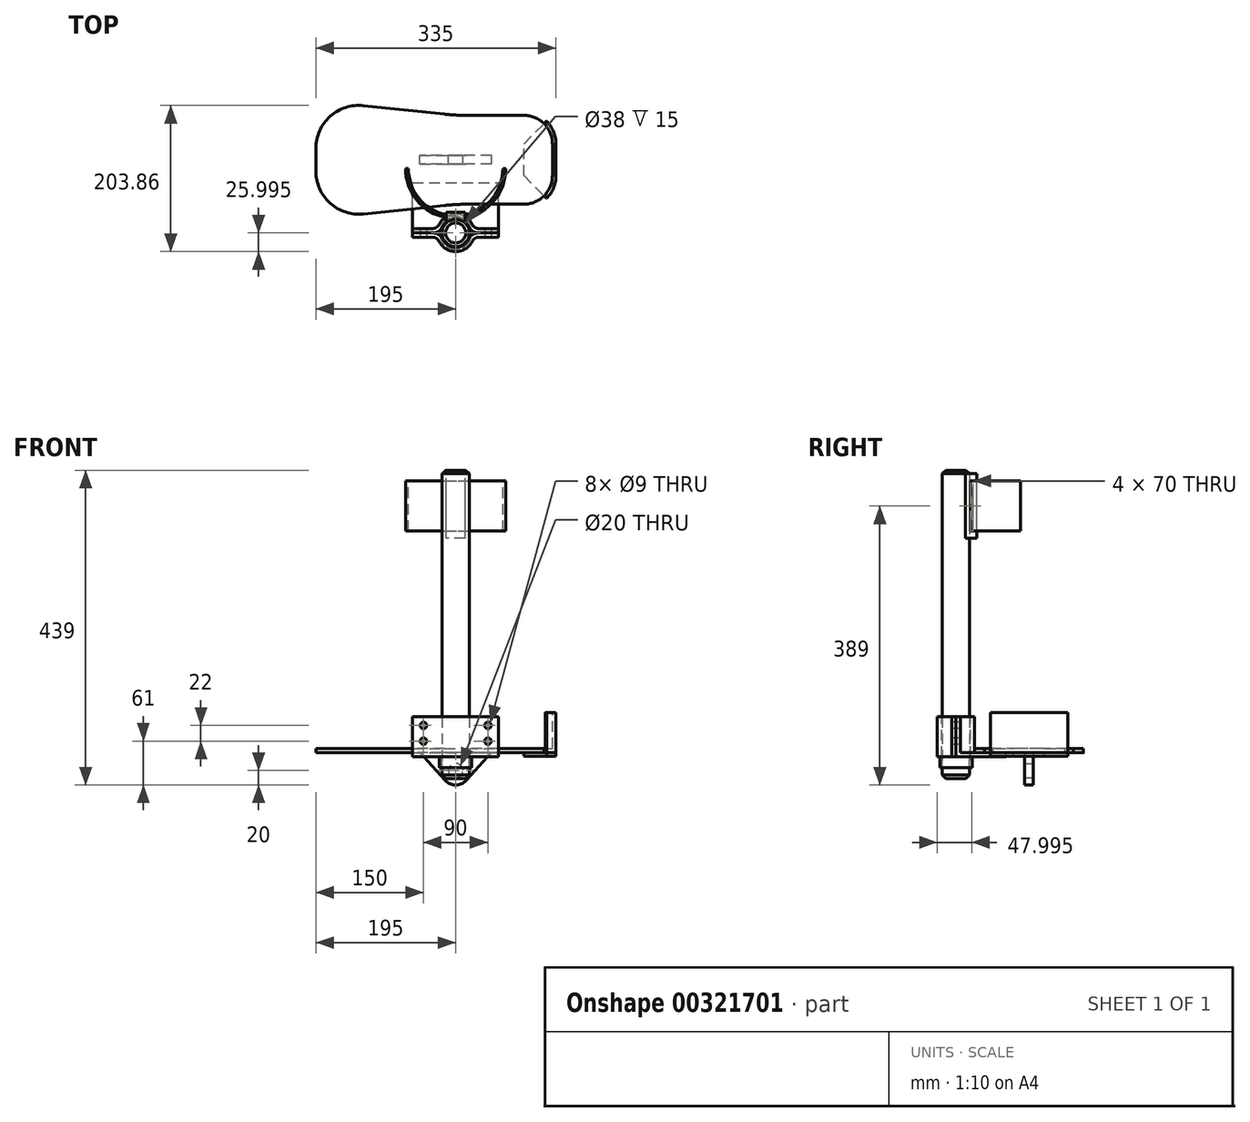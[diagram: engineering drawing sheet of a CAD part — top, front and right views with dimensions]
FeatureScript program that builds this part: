
annotation { "Feature Type Name" : "Feature", "Feature Type Description" : "" }
export const myFeature = defineFeature(function(context is Context, id is Id, definition is map)
    precondition{}
    {
        {
            var Q0;
            Q0=qCreatedBy(makeId("Top.planeOp"),FACE);
            var sketch = newSketch(context, id + "F0", { "sketchPlane" : qUnion([Q0])});
            skLineSegment(sketch, "E0", {"start": v(-175, 82.5) * mm, "end": v(-175, -82.5) * mm});
            skLineSegment(sketch, "E1", {"start": v(-175, 82.5) * mm, "end": v(20, 62) * mm});
            skLineSegment(sketch, "E2", {"start": v(20, 62) * mm, "end": v(155, 62) * mm});
            skLineSegment(sketch, "E3", {"start": v(155, 62) * mm, "end": v(155, -62) * mm});
            skLineSegment(sketch, "E4", {"start": v(155, -62) * mm, "end": v(20, -62) * mm});
            skLineSegment(sketch, "E5", {"start": v(20, -62) * mm, "end": v(-175, -82.5) * mm});
            skSolve(sketch);
        }
        {
            var Q0;
            Q0=makeQuery(id+"F0.imprint","IMPRINT",FACE,{"disambiguationData":[TD([[makeQuery(id+"F0.imprint","IMPRINT",EDGE,{"derivedFrom":sQuery(id+"F0.wireOp",EDGE,"E0")}),1.0]])]});
            extrude(context, id + "F1", {"entities" : qUnion([Q0]), "depth" : 6 * mm});
        }
        {
            var Q0;
            Q0=makeQuery(id+"F1.opExtrude","SWEPT_EDGE",EDGE,{"disambiguationData":[OSD([sQuery(id+"F0.wireOp",EDGE,"E0"),sQuery(id+"F0.wireOp",EDGE,"E5")])]});
            var Q1;
            Q1=makeQuery(id+"F1.opExtrude","SWEPT_EDGE",EDGE,{"disambiguationData":[OSD([sQuery(id+"F0.wireOp",EDGE,"E0"),sQuery(id+"F0.wireOp",EDGE,"E1")])]});
            fillet(context, id + "F2", {"entities" : qUnion([Q0, Q1]), "radius" : 60 * mm, "tangentPropagation" : true, "allowEdgeOverflow" : false});
        }
        {
            var Q0;
            Q0=makeQuery(id+"F1.opExtrude","SWEPT_EDGE",EDGE,{"disambiguationData":[OSD([sQuery(id+"F0.wireOp",EDGE,"E2"),sQuery(id+"F0.wireOp",EDGE,"E3")])]});
            var Q1;
            Q1=makeQuery(id+"F1.opExtrude","SWEPT_EDGE",EDGE,{"disambiguationData":[OSD([sQuery(id+"F0.wireOp",EDGE,"E3"),sQuery(id+"F0.wireOp",EDGE,"E4")])]});
            fillet(context, id + "F3", {"entities" : qUnion([Q0, Q1]), "radius" : 40 * mm, "tangentPropagation" : true, "allowEdgeOverflow" : false});
        }
        {
            var Q0;
            Q0=makeQuery(id+"F1.opExtrude","SWEPT_EDGE",EDGE,{"disambiguationData":[OSD([sQuery(id+"F0.wireOp",EDGE,"E4"),sQuery(id+"F0.wireOp",EDGE,"E5")])]});
            var Q1;
            Q1=makeQuery(id+"F1.opExtrude","SWEPT_EDGE",EDGE,{"disambiguationData":[OSD([sQuery(id+"F0.wireOp",EDGE,"E1"),sQuery(id+"F0.wireOp",EDGE,"E2")])]});
            fillet(context, id + "F4", {"entities" : qUnion([Q0, Q1]), "radius" : 300 * mm, "tangentPropagation" : true, "allowEdgeOverflow" : false});
        }
        {
            var Q0;
            Q0=qCreatedBy(makeId("Front.planeOp"),FACE);
            var sketch = newSketch(context, id + "F5", { "sketchPlane" : qUnion([Q0])});
            skArc(sketch, "E6", {"start": v(5.25, -38.5) * mm, "mid": v(20, -45) * mm, "end": v(34.75, -38.5) * mm});
            skLineSegment(sketch, "E7", {"start": v(20, -25) * mm, "end": v(20, 19.27) * mm, "construction": true});
            skLineSegment(sketch, "E8.0", {"start": v(70, -25) * mm, "end": v(70, 0) * mm, "construction": true});
            skLineSegment(sketch, "E9.0", {"start": v(-30, -25) * mm, "end": v(-30, 0) * mm, "construction": true});
            skLineSegment(sketch, "E10.0", {"start": v(70, 0) * mm, "end": v(-30, 0) * mm});
            skPoint(sketch, "E11.orphan", {"position": v(4.36, 0) * mm});
            skPoint(sketch, "E12.orphan", {"position": v(-108.73, 0) * mm});
            skLineSegment(sketch, "E13", {"start": v(-30, 0) * mm, "end": v(5.25, -38.5) * mm});
            skLineSegment(sketch, "E14", {"start": v(70, 0) * mm, "end": v(34.75, -38.5) * mm});
            skCircle(sketch, "E15", {"center": v(20, -25) * mm, "radius": 10 * mm});
            skSolve(sketch);
        }
        {
            var Q0;
            Q0=makeQuery(id+"F5.imprint","IMPRINT",FACE,{"disambiguationData":[TD([[makeQuery(id+"F5.imprint","IMPRINT",EDGE,{"derivedFrom":sQuery(id+"F5.wireOp",EDGE,"E6")}),1.0]])]});
            extrude(context, id + "F6", {"entities" : qUnion([Q0]), "operationType" : NewBodyOperationType.ADD, "endBound" : BoundingType.SYMMETRIC, "depth" : 12 * mm});
        }
        {
            var Q0;
            Q0=makeQuery(id+"F1.opExtrude","CAP_FACE",FACE,{"disambiguationData":[OSD([sQuery(id+"F0.wireOp",EDGE,"E0"),sQuery(id+"F0.wireOp",EDGE,"E1"),sQuery(id+"F0.wireOp",EDGE,"E2"),sQuery(id+"F0.wireOp",EDGE,"E3"),sQuery(id+"F0.wireOp",EDGE,"E4"),sQuery(id+"F0.wireOp",EDGE,"E5")])],"isStart":false});
            var sketch = newSketch(context, id + "F7", { "sketchPlane" : qUnion([Q0])});
            skLineSegment(sketch, "E16.0", {"start": v(155, 22) * mm, "end": v(155, -22) * mm});
            skArc(sketch, "E17.0", {"start": v(155, 22) * mm, "mid": v(151.96, 37.31) * mm, "end": v(143.28, 50.29) * mm});
            skArc(sketch, "E18.0", {"start": v(143.28, -50.29) * mm, "mid": v(151.96, -37.31) * mm, "end": v(155, -22) * mm});
            skLineSegment(sketch, "E19", {"start": v(143.28, 50.29) * mm, "end": v(146.82, 53.82) * mm});
            skLineSegment(sketch, "E20", {"start": v(143.28, -50.29) * mm, "end": v(146.82, -53.82) * mm});
            skPoint(sketch, "E21.orphan", {"position": v(115, 62) * mm});
            skPoint(sketch, "E22.orphan", {"position": v(115, -62) * mm});
            skArc(sketch, "E23.0", {"start": v(160, 22) * mm, "mid": v(156.57, 39.23) * mm, "end": v(146.82, 53.82) * mm});
            skLineSegment(sketch, "E23.1", {"start": v(160, 22) * mm, "end": v(160, -22) * mm});
            skArc(sketch, "E23.2", {"start": v(146.82, -53.82) * mm, "mid": v(156.57, -39.23) * mm, "end": v(160, -22) * mm});
            skSolve(sketch);
        }
        {
            var Q0;
            Q0=makeQuery(id+"F7.imprint","IMPRINT",FACE,{"disambiguationData":[TD([[makeQuery(id+"F7.imprint","IMPRINT",EDGE,{"derivedFrom":sQuery(id+"F7.wireOp",EDGE,"E16.0")}),1.0]])]});
            extrude(context, id + "F8", {"entities" : qUnion([Q0]), "oppositeDirection" : true, "depth" : 6 * mm});
        }
        {
            var Q0;
            Q0 = qSketchRegion(id + "F7", true);
            extrude(context, id + "F9", {"entities" : qUnion([Q0]), "operationType" : NewBodyOperationType.ADD, "depth" : 50 * mm});
        }
        {
            var Q0;
            {var subQ0=sQuery(id+"F7.wireOp",EDGE,"E20");var subQ1=sQuery(id+"F7.wireOp",EDGE,"E18.0");var subQ2=sQuery(id+"F0.wireOp",EDGE,"E5");var subQ3=sQuery(id+"F0.wireOp",EDGE,"E4");var subQ4=sQuery(id+"F0.wireOp",EDGE,"E3");var subQ5=sQuery(id+"F0.wireOp",EDGE,"E2");var subQ6=sQuery(id+"F0.wireOp",EDGE,"E1");var subQ7=sQuery(id+"F0.wireOp",EDGE,"E0");Q0=makeQuery(id+"F9.boolean.opBoolean","MERGE",EDGE,{"derivedFrom":[makeQuery(id+"F8.opExtrude","SWEPT_EDGE",EDGE,{"disambiguationData":[OSD([subQ7,subQ6,subQ5,subQ4,subQ3,subQ2,subQ1,subQ0])]}),makeQuery(id+"F9.opExtrude","SWEPT_EDGE",EDGE,{"disambiguationData":[OSD([subQ7,subQ6,subQ5,subQ4,subQ3,subQ2,subQ1,subQ0])]})]});}
            var Q1;
            {var subQ0=sQuery(id+"F7.wireOp",EDGE,"E19");var subQ1=sQuery(id+"F7.wireOp",EDGE,"E17.0");var subQ2=sQuery(id+"F0.wireOp",EDGE,"E5");var subQ3=sQuery(id+"F0.wireOp",EDGE,"E4");var subQ4=sQuery(id+"F0.wireOp",EDGE,"E3");var subQ5=sQuery(id+"F0.wireOp",EDGE,"E2");var subQ6=sQuery(id+"F0.wireOp",EDGE,"E1");var subQ7=sQuery(id+"F0.wireOp",EDGE,"E0");Q1=makeQuery(id+"F9.boolean.opBoolean","MERGE",EDGE,{"derivedFrom":[makeQuery(id+"F8.opExtrude","SWEPT_EDGE",EDGE,{"disambiguationData":[OSD([subQ7,subQ6,subQ5,subQ4,subQ3,subQ2,subQ1,subQ0])]}),makeQuery(id+"F9.opExtrude","SWEPT_EDGE",EDGE,{"disambiguationData":[OSD([subQ7,subQ6,subQ5,subQ4,subQ3,subQ2,subQ1,subQ0])]})]});}
            fillet(context, id + "F10", {"entities" : qUnion([Q0, Q1]), "radius" : 5 * mm, "tangentPropagation" : true, "allowEdgeOverflow" : false});
        }
        {
            var Q0;
            Q0=makeQuery(id+"F8.opExtrude","CAP_FACE",FACE,{"disambiguationData":[OSD([sQuery(id+"F7.wireOp",EDGE,"E16.0"),sQuery(id+"F7.wireOp",EDGE,"E17.0"),sQuery(id+"F7.wireOp",EDGE,"E18.0"),sQuery(id+"F7.wireOp",EDGE,"E19"),sQuery(id+"F7.wireOp",EDGE,"E20"),sQuery(id+"F7.wireOp",EDGE,"E23.0"),sQuery(id+"F7.wireOp",EDGE,"E23.1"),sQuery(id+"F7.wireOp",EDGE,"E23.2")])],"isStart":false});
            var sketch = newSketch(context, id + "F11", { "sketchPlane" : qUnion([Q0])});
            skArc(sketch, "E24.0", {"start": v(146.82, 53.82) * mm, "mid": v(156.57, 39.23) * mm, "end": v(160, 22) * mm});
            skLineSegment(sketch, "E25.0", {"start": v(160, -22) * mm, "end": v(160, 22) * mm});
            skArc(sketch, "E26.0", {"start": v(160, -22) * mm, "mid": v(156.57, -39.23) * mm, "end": v(146.82, -53.82) * mm});
            skLineSegment(sketch, "E27", {"start": v(115, 22) * mm, "end": v(146.82, 53.82) * mm});
            skLineSegment(sketch, "E28", {"start": v(115, 22) * mm, "end": v(115, -22) * mm});
            skLineSegment(sketch, "E29", {"start": v(115, -22) * mm, "end": v(146.82, -53.82) * mm});
            skSolve(sketch);
        }
        {
            var Q0;
            Q0 = qSketchRegion(id + "F11", true);
            extrude(context, id + "F12", {"entities" : qUnion([Q0]), "depth" : 5 * mm});
        }
        {
            var Q0;
            Q0=makeQuery(id+"F1.opExtrude","CAP_FACE",FACE,{"disambiguationData":[OSD([sQuery(id+"F0.wireOp",EDGE,"E0"),sQuery(id+"F0.wireOp",EDGE,"E1"),sQuery(id+"F0.wireOp",EDGE,"E2"),sQuery(id+"F0.wireOp",EDGE,"E3"),sQuery(id+"F0.wireOp",EDGE,"E4"),sQuery(id+"F0.wireOp",EDGE,"E5")])],"isStart":true});
            var sketch = newSketch(context, id + "F13", { "sketchPlane" : qUnion([Q0])});
            skLineSegment(sketch, "E30.bottom", {"start": v(-40, 102) * mm, "end": v(0, 102) * mm});
            skLineSegment(sketch, "E30.top", {"start": v(-40, 32) * mm, "end": v(80, 32) * mm});
            skLineSegment(sketch, "E30.left", {"start": v(-40, 102) * mm, "end": v(-40, 32) * mm});
            skLineSegment(sketch, "E30.right", {"start": v(80, 102) * mm, "end": v(80, 32) * mm});
            skArc(sketch, "E31", {"start": v(0, 102) * mm, "mid": v(20, 82) * mm, "end": v(40, 102) * mm});
            skLineSegment(sketch, "E32.trimOffspring", {"start": v(40, 102) * mm, "end": v(80, 102) * mm});
            skSolve(sketch);
        }
        {
            var Q0;
            {var subQ8=sQuery(id+"F13.wireOp",EDGE,"E30.bottom");Q0=makeQuery(id+"F13.imprint","IMPRINT",FACE,{"disambiguationData":[TD([[makeQuery(id+"F13.imprint","IMPRINT",EDGE,{"derivedFrom":subQ8}),-1.0]])]});}
            var Q1;
            {var subQ4=sQuery(id+"F13.wireOp",EDGE,"E30.top");Q1=makeQuery(id+"F13.imprint","IMPRINT",FACE,{"disambiguationData":[TD([[makeQuery(id+"F13.imprint","IMPRINT",EDGE,{"derivedFrom":subQ4}),1.0]])]});}
            extrude(context, id + "F14", {"entities" : qUnion([Q0, Q1]), "depth" : 6 * mm});
        }
        {
            var Q0;
            Q0=makeQuery(id+"F14.opExtrude","CAP_FACE",FACE,{"disambiguationData":[OSD([sQuery(id+"F13.wireOp",EDGE,"E30.bottom"),sQuery(id+"F13.wireOp",EDGE,"E30.top"),sQuery(id+"F13.wireOp",EDGE,"E30.left"),sQuery(id+"F13.wireOp",EDGE,"E30.right"),sQuery(id+"F13.wireOp",EDGE,"E31"),sQuery(id+"F13.wireOp",EDGE,"E32.trimOffspring")])],"isStart":true});
            var sketch = newSketch(context, id + "F15", { "sketchPlane" : qUnion([Q0])});
            skArc(sketch, "E33.0", {"start": v(0, -102) * mm, "mid": v(20, -82) * mm, "end": v(40, -102) * mm});
            skLineSegment(sketch, "E34.0", {"start": v(-40, -102) * mm, "end": v(0, -102) * mm});
            skLineSegment(sketch, "E35.0", {"start": v(40, -102) * mm, "end": v(80, -102) * mm});
            skLineSegment(sketch, "E36.0", {"start": v(45.3, -96) * mm, "end": v(80, -96) * mm});
            skArc(sketch, "E36.1", {"start": v(-5.3, -96) * mm, "mid": v(20, -76) * mm, "end": v(45.3, -96) * mm});
            skLineSegment(sketch, "E36.2", {"start": v(-40, -96) * mm, "end": v(-5.3, -96) * mm});
            skLineSegment(sketch, "E37", {"start": v(-40, -96) * mm, "end": v(-40, -102) * mm});
            skLineSegment(sketch, "E38", {"start": v(80, -96) * mm, "end": v(80, -102) * mm});
            skSolve(sketch);
        }
        {
            var Q0;
            Q0=makeQuery(id+"F15.imprint","IMPRINT",FACE,{"disambiguationData":[TD([[makeQuery(id+"F15.imprint","IMPRINT",EDGE,{"derivedFrom":sQuery(id+"F15.wireOp",EDGE,"E33.0")}),1.0]])]});
            extrude(context, id + "F16", {"entities" : qUnion([Q0]), "operationType" : NewBodyOperationType.ADD, "depth" : 50 * mm});
        }
        {
            var Q0;
            Q0=makeQuery(id+"F16.opExtrude","SWEPT_EDGE",EDGE,{"disambiguationData":[OSD([sQuery(id+"F15.wireOp",EDGE,"E36.1"),sQuery(id+"F15.wireOp",EDGE,"E36.2")])]});
            var Q1;
            Q1=makeQuery(id+"F16.opExtrude","SWEPT_EDGE",EDGE,{"disambiguationData":[OSD([sQuery(id+"F15.wireOp",EDGE,"E36.0"),sQuery(id+"F15.wireOp",EDGE,"E36.1")])]});
            fillet(context, id + "F17", {"entities" : qUnion([Q0, Q1]), "radius" : 10 * mm, "tangentPropagation" : true, "allowEdgeOverflow" : false});
        }
        {
            var Q0;
            Q0=makeQuery(id+"F16.boolean.opBoolean","MERGE",EDGE,{"derivedFrom":[makeQuery(id+"F14.opExtrude","SWEPT_EDGE",EDGE,{"disambiguationData":[OSD([sQuery(id+"F13.wireOp",EDGE,"E31"),sQuery(id+"F13.wireOp",EDGE,"E32.trimOffspring")])]}),makeQuery(id+"F16.opExtrude","SWEPT_EDGE",EDGE,{"disambiguationData":[OSD([sQuery(id+"F15.wireOp",EDGE,"E33.0"),sQuery(id+"F15.wireOp",EDGE,"E35.0")])]})]});
            var Q1;
            Q1=makeQuery(id+"F16.boolean.opBoolean","MERGE",EDGE,{"derivedFrom":[makeQuery(id+"F14.opExtrude","SWEPT_EDGE",EDGE,{"disambiguationData":[OSD([sQuery(id+"F13.wireOp",EDGE,"E30.bottom"),sQuery(id+"F13.wireOp",EDGE,"E31")])]}),makeQuery(id+"F16.opExtrude","SWEPT_EDGE",EDGE,{"disambiguationData":[OSD([sQuery(id+"F15.wireOp",EDGE,"E33.0"),sQuery(id+"F15.wireOp",EDGE,"E34.0")])]})]});
            fillet(context, id + "F18", {"entities" : qUnion([Q0, Q1]), "radius" : 15 * mm, "tangentPropagation" : true, "allowEdgeOverflow" : false});
        }
        {
            var Q0;
            Q0=makeQuery(id+"F16.opExtrude","CAP_FACE",FACE,{"disambiguationData":[OSD([sQuery(id+"F15.wireOp",EDGE,"E33.0"),sQuery(id+"F15.wireOp",EDGE,"E34.0"),sQuery(id+"F15.wireOp",EDGE,"E35.0"),sQuery(id+"F15.wireOp",EDGE,"E36.0"),sQuery(id+"F15.wireOp",EDGE,"E36.1"),sQuery(id+"F15.wireOp",EDGE,"E36.2"),sQuery(id+"F15.wireOp",EDGE,"E37"),sQuery(id+"F15.wireOp",EDGE,"E38")])],"isStart":false});
            var sketch = newSketch(context, id + "F19", { "sketchPlane" : qUnion([Q0])});
            skLineSegment(sketch, "E39.0", {"start": v(-40, -102) * mm, "end": v(-11.62, -102) * mm});
            skArc(sketch, "E40.0", {"start": v(-11.62, -102) * mm, "mid": v(-3.6, -99.68) * mm, "end": v(1.93, -93.43) * mm, "construction": true});
            skArc(sketch, "E41.0", {"start": v(1.93, -93.43) * mm, "mid": v(20, -82) * mm, "end": v(38.07, -93.43) * mm, "construction": true});
            skArc(sketch, "E42.0", {"start": v(38.07, -93.43) * mm, "mid": v(43.6, -99.68) * mm, "end": v(51.62, -102) * mm, "construction": true});
            skLineSegment(sketch, "E43.0", {"start": v(51.62, -102) * mm, "end": v(80, -102) * mm});
            skLineSegment(sketch, "E44.0", {"start": v(-40, -96) * mm, "end": v(-12.25, -96) * mm, "construction": true});
            skArc(sketch, "E45.0", {"start": v(-3.3, -90.45) * mm, "mid": v(-6.98, -94.5) * mm, "end": v(-12.25, -96) * mm, "construction": true});
            skArc(sketch, "E46.0", {"start": v(-3.3, -90.45) * mm, "mid": v(20, -76) * mm, "end": v(43.3, -90.45) * mm, "construction": true});
            skArc(sketch, "E47.0", {"start": v(52.25, -96) * mm, "mid": v(46.98, -94.5) * mm, "end": v(43.3, -90.45) * mm, "construction": true});
            skLineSegment(sketch, "E48.0", {"start": v(52.25, -96) * mm, "end": v(80, -96) * mm, "construction": true});
            skLineSegment(sketch, "E49.0", {"start": v(-40, -102) * mm, "end": v(-40, -96) * mm, "construction": true});
            skLineSegment(sketch, "E50.0", {"start": v(80, -102) * mm, "end": v(80, -96) * mm, "construction": true});
            skLineSegment(sketch, "E51.MirrorCS", {"start": v(80, -102) * mm, "end": v(80, -108) * mm});
            skLineSegment(sketch, "E52.MirrorCS", {"start": v(-40, -102) * mm, "end": v(-40, -108) * mm});
            skArc(sketch, "E53.MirrorCS", {"start": v(-11.62, -102) * mm, "mid": v(-3.6, -104.33) * mm, "end": v(1.93, -110.58) * mm});
            skArc(sketch, "E54.MirrorCS", {"start": v(1.93, -110.58) * mm, "mid": v(20, -122) * mm, "end": v(38.07, -110.58) * mm});
            skArc(sketch, "E55.MirrorCS", {"start": v(38.07, -110.58) * mm, "mid": v(43.6, -104.33) * mm, "end": v(51.62, -102) * mm});
            skLineSegment(sketch, "E56.MirrorCS", {"start": v(-40, -108) * mm, "end": v(-12.25, -108) * mm});
            skLineSegment(sketch, "E57.MirrorCS", {"start": v(52.25, -108) * mm, "end": v(80, -108) * mm});
            skArc(sketch, "E58.MirrorCS", {"start": v(52.25, -108) * mm, "mid": v(46.98, -109.5) * mm, "end": v(43.3, -113.56) * mm});
            skArc(sketch, "E59.MirrorCS", {"start": v(-3.3, -113.56) * mm, "mid": v(20, -128) * mm, "end": v(43.3, -113.56) * mm});
            skArc(sketch, "E60.MirrorCS", {"start": v(-3.3, -113.56) * mm, "mid": v(-6.98, -109.5) * mm, "end": v(-12.25, -108) * mm});
            skSolve(sketch);
        }
        {
            var Q0;
            Q0=makeQuery(id+"F19.imprint","IMPRINT",FACE,{"disambiguationData":[TD([[makeQuery(id+"F19.imprint","IMPRINT",EDGE,{"derivedFrom":sQuery(id+"F19.wireOp",EDGE,"E39.0")}),-1.0]])]});
            extrude(context, id + "F20", {"entities" : qUnion([Q0]), "oppositeDirection" : true, "depth" : 56 * mm});
        }
        {
            var Q0;
            Q0=makeQuery(id+"F20.opExtrude","SWEPT_FACE",FACE,{"disambiguationData":[OSD([sQuery(id+"F19.wireOp",EDGE,"E56.MirrorCS")])]});
            var sketch = newSketch(context, id + "F21", { "sketchPlane" : qUnion([Q0])});
            skCircle(sketch, "E61", {"center": v(-25, 38) * mm, "radius": 4.5 * mm});
            skPoint(sketch, "E61.centerSnap0", {"position": v(-26.12, 50) * mm});
            skCircle(sketch, "E62", {"center": v(-25, 16) * mm, "radius": 4.5 * mm});
            skCircle(sketch, "E63", {"center": v(65, 38) * mm, "radius": 4.5 * mm});
            skCircle(sketch, "E64", {"center": v(65, 16) * mm, "radius": 4.5 * mm});
            skSolve(sketch);
        }
        {
            var Q0;
            Q0 = qSketchRegion(id + "F21", true);
            extrude(context, id + "F22", {"entities" : qUnion([Q0]), "operationType" : NewBodyOperationType.REMOVE, "oppositeDirection" : true, "depth" : 25 * mm});
        }
        {
            var Q0;
            Q0=makeQuery(id+"F16.opExtrude","SWEPT_FACE",FACE,{"disambiguationData":[OSD([sQuery(id+"F15.wireOp",EDGE,"E36.2")])]});
            var sketch = newSketch(context, id + "F23", { "sketchPlane" : qUnion([Q0])});
            skCircle(sketch, "E65.0", {"center": v(25, 38) * mm, "radius": 4.5 * mm});
            skPoint(sketch, "E65.1", {"position": v(26.12, 50) * mm});
            skCircle(sketch, "E65.2", {"center": v(25, 16) * mm, "radius": 4.5 * mm});
            skCircle(sketch, "E65.3", {"center": v(-65, 38) * mm, "radius": 4.5 * mm});
            skCircle(sketch, "E65.4", {"center": v(-65, 16) * mm, "radius": 4.5 * mm});
            skSolve(sketch);
        }
        {
            var Q0;
            Q0 = qSketchRegion(id + "F23", true);
            extrude(context, id + "F24", {"entities" : qUnion([Q0]), "operationType" : NewBodyOperationType.REMOVE, "oppositeDirection" : true, "depth" : 25 * mm});
        }
        {
            var Q0;
            Q0=makeQuery(id+"F14.opExtrude","CAP_FACE",FACE,{"disambiguationData":[OSD([sQuery(id+"F13.wireOp",EDGE,"E30.bottom"),sQuery(id+"F13.wireOp",EDGE,"E30.top"),sQuery(id+"F13.wireOp",EDGE,"E30.left"),sQuery(id+"F13.wireOp",EDGE,"E30.right"),sQuery(id+"F13.wireOp",EDGE,"E31"),sQuery(id+"F13.wireOp",EDGE,"E32.trimOffspring")])],"isStart":false});
            var sketch = newSketch(context, id + "F25", { "sketchPlane" : qUnion([Q0])});
            skArc(sketch, "E66.0", {"start": v(1.93, 93.43) * mm, "mid": v(20, 82) * mm, "end": v(38.07, 93.43) * mm, "construction": true});
            skCircle(sketch, "E67", {"center": v(20, 102) * mm, "radius": 19 * mm});
            skSolve(sketch);
        }
        {
            var Q0;
            Q0=makeQuery(id+"F25.imprint","IMPRINT",FACE,{"disambiguationData":[TD([[makeQuery(id+"F25.imprint","IMPRINT",EDGE,{"derivedFrom":sQuery(id+"F25.wireOp",EDGE,"E67")}),1.0]])]});
            extrude(context, id + "F26", {"entities" : qUnion([Q0]), "oppositeDirection" : true, "depth" : 400 * mm});
        }
        {
            var Q0;
            Q0=makeQuery(id+"F26.opExtrude","CAP_FACE",FACE,{"disambiguationData":[OSD([sQuery(id+"F25.wireOp",EDGE,"E67")])],"isStart":true});
            extrude(context, id + "F27", {"entities" : qUnion([Q0]), "operationType" : NewBodyOperationType.ADD, "depth" : 30 * mm});
        }
        {
            var Q0;
            Q0=makeQuery(id+"F27.opExtrude","CAP_EDGE",EDGE,{"disambiguationData":[OSD([sQuery(id+"F25.wireOp",EDGE,"E67")])],"isStart":false});
            chamfer(context, id + "F28", {"entities" : qUnion([Q0]), "width" : 5 * mm, "tangentPropagation" : true});
        }
        {
            var Q0;
            Q0=makeQuery(id+"F14.opExtrude","CAP_FACE",FACE,{"disambiguationData":[OSD([sQuery(id+"F13.wireOp",EDGE,"E30.bottom"),sQuery(id+"F13.wireOp",EDGE,"E30.top"),sQuery(id+"F13.wireOp",EDGE,"E30.left"),sQuery(id+"F13.wireOp",EDGE,"E30.right"),sQuery(id+"F13.wireOp",EDGE,"E31"),sQuery(id+"F13.wireOp",EDGE,"E32.trimOffspring")])],"isStart":false});
            var sketch = newSketch(context, id + "F29", { "sketchPlane" : qUnion([Q0])});
            skCircle(sketch, "E68.0", {"center": v(20, 102) * mm, "radius": 19 * mm});
            skCircle(sketch, "E69", {"center": v(20, 102) * mm, "radius": 22.5 * mm});
            skSolve(sketch);
        }
        {
            var Q0;
            Q0 = qSketchRegion(id + "F29", true);
            extrude(context, id + "F30", {"entities" : qUnion([Q0]), "depth" : 15 * mm});
        }
        {
            var Q0;
            Q0=makeQuery(id+"F26.opExtrude","CAP_EDGE",EDGE,{"disambiguationData":[OSD([sQuery(id+"F25.wireOp",EDGE,"E67")])],"isStart":false});
            chamfer(context, id + "F31", {"entities" : qUnion([Q0]), "width" : 5 * mm, "tangentPropagation" : true});
        }
        {
            var Q0;
            Q0=makeQuery(id+"F26.opExtrude","CAP_FACE",FACE,{"disambiguationData":[OSD([sQuery(id+"F25.wireOp",EDGE,"E67")])],"isStart":false});
            cPlane(context, id + "F32", {"entities" : qUnion([Q0]), "cplaneType" : CPlaneType.OFFSET, "offset" : 5 * mm, "oppositeDirection" : true, "width" : 150 * mm, "height" : 150 * mm});
        }
        {
            var Q0;
            Q0=qCreatedBy(id+"F32.planeOp",FACE);
            var sketch = newSketch(context, id + "F33", { "sketchPlane" : qUnion([Q0])});
            skArc(sketch, "E70.0", {"start": v(6.56, -115.44) * mm, "mid": v(20, -121) * mm, "end": v(33.44, -115.44) * mm});
            skLineSegment(sketch, "E71", {"start": v(20, -102) * mm, "end": v(33.44, -115.44) * mm, "construction": true});
            skLineSegment(sketch, "E72", {"start": v(20, -102) * mm, "end": v(6.56, -115.44) * mm, "construction": true});
            skLineSegment(sketch, "E73", {"start": v(20, -102) * mm, "end": v(20, -121) * mm, "construction": true});
            skLineSegment(sketch, "E74", {"start": v(33.44, -115.44) * mm, "end": v(33.44, -131) * mm, "construction": true});
            skLineSegment(sketch, "E75", {"start": v(6.56, -115.44) * mm, "end": v(6.56, -131) * mm, "construction": true});
            skLineSegment(sketch, "E76", {"start": v(33.44, -131) * mm, "end": v(6.56, -131) * mm, "construction": true});
            skPoint(sketch, "E76.endSnap0", {"position": v(20, -131) * mm});
            skPoint(sketch, "E77.orphan", {"position": v(3.56, -131) * mm});
            skLineSegment(sketch, "E78", {"start": v(20, -102) * mm, "end": v(-17.7, -102) * mm, "construction": true});
            skPoint(sketch, "E79.MirrorP", {"position": v(20, -73) * mm});
            skLineSegment(sketch, "E80.MirrorCS", {"start": v(33.44, -73) * mm, "end": v(6.56, -73) * mm});
            skLineSegment(sketch, "E81.MirrorCS", {"start": v(20, -102) * mm, "end": v(6.56, -88.57) * mm, "construction": true});
            skLineSegment(sketch, "E82.MirrorCS", {"start": v(33.44, -88.57) * mm, "end": v(33.44, -73) * mm});
            skPoint(sketch, "E83.MirrorP", {"position": v(3.56, -73) * mm});
            skLineSegment(sketch, "E84.MirrorCS", {"start": v(20, -102) * mm, "end": v(33.44, -88.57) * mm, "construction": true});
            skLineSegment(sketch, "E85.MirrorCS", {"start": v(20, -102) * mm, "end": v(20, -83) * mm, "construction": true});
            skLineSegment(sketch, "E86.MirrorCS", {"start": v(6.56, -88.57) * mm, "end": v(6.56, -73) * mm});
            skArc(sketch, "E87.MirrorCS", {"start": v(6.56, -88.57) * mm, "mid": v(20, -83) * mm, "end": v(33.44, -88.57) * mm});
            skSolve(sketch);
        }
        {
            var Q0;
            Q0=makeQuery(id+"F33.imprint","IMPRINT",FACE,{"disambiguationData":[TD([[makeQuery(id+"F33.imprint","IMPRINT",EDGE,{"derivedFrom":sQuery(id+"F33.wireOp",EDGE,"E80.MirrorCS")}),1.0]])]});
            extrude(context, id + "F34", {"entities" : qUnion([Q0]), "oppositeDirection" : true, "depth" : 90 * mm});
        }
        {
            var Q0;
            Q0=makeQuery(id+"F34.opExtrude","CAP_FACE",FACE,{"disambiguationData":[OSD([sQuery(id+"F33.wireOp",EDGE,"E70.0"),sQuery(id+"F33.wireOp",EDGE,"6aff0cf1-5d87-4cb3-9122-d07783136f99.0"),sQuery(id+"F33.wireOp",EDGE,"E74"),sQuery(id+"F33.wireOp",EDGE,"E75")])],"isStart":true});
            var Q1;
            Q1=makeQuery(id+"F34.opExtrude","CAP_FACE",FACE,{"disambiguationData":[OSD([sQuery(id+"F33.wireOp",EDGE,"E80.MirrorCS"),sQuery(id+"F33.wireOp",EDGE,"E82.MirrorCS"),sQuery(id+"F33.wireOp",EDGE,"E86.MirrorCS"),sQuery(id+"F33.wireOp",EDGE,"E87.MirrorCS")])],"isStart":true});
            cPlane(context, id + "F35", {"entities" : qUnion([Q0, Q1]), "cplaneType" : CPlaneType.OFFSET, "offset" : 10 * mm, "oppositeDirection" : true, "width" : 150 * mm, "height" : 150 * mm});
        }
        {
            var Q0;
            Q0=qCreatedBy(id+"F35.planeOp",FACE);
            var sketch = newSketch(context, id + "F36", { "sketchPlane" : qUnion([Q0])});
            skLineSegment(sketch, "E88.0", {"start": v(6.56, -115.44) * mm, "end": v(6.56, -131) * mm, "construction": true});
            skLineSegment(sketch, "E89.0", {"start": v(33.44, -115.44) * mm, "end": v(33.44, -131) * mm, "construction": true});
            skLineSegment(sketch, "E90.bottom", {"start": v(6.56, -126) * mm, "end": v(33.44, -126) * mm, "construction": true});
            skLineSegment(sketch, "E90.top", {"start": v(6.56, -122) * mm, "end": v(33.44, -122) * mm, "construction": true});
            skLineSegment(sketch, "E90.left", {"start": v(6.56, -126) * mm, "end": v(6.56, -122) * mm, "construction": true});
            skLineSegment(sketch, "E90.right", {"start": v(33.44, -126) * mm, "end": v(33.44, -122) * mm, "construction": true});
            skCircle(sketch, "E91.0", {"center": v(20, -102) * mm, "radius": 14 * mm, "construction": true});
            skLineSegment(sketch, "E92", {"start": v(20, -102) * mm, "end": v(-60.22, -102) * mm, "construction": true});
            skLineSegment(sketch, "E93.MirrorCS", {"start": v(33.44, -78) * mm, "end": v(33.44, -82) * mm});
            skLineSegment(sketch, "E94.MirrorCS", {"start": v(6.56, -78) * mm, "end": v(6.56, -82) * mm});
            skLineSegment(sketch, "E95.MirrorCS", {"start": v(33.44, -88.57) * mm, "end": v(33.44, -73) * mm, "construction": true});
            skLineSegment(sketch, "E96.MirrorCS", {"start": v(6.56, -88.57) * mm, "end": v(6.56, -73) * mm, "construction": true});
            skLineSegment(sketch, "E97.MirrorCS", {"start": v(6.56, -82) * mm, "end": v(33.44, -82) * mm});
            skLineSegment(sketch, "E98.MirrorCS", {"start": v(6.56, -78) * mm, "end": v(33.44, -78) * mm});
            skSolve(sketch);
        }
        {
            var Q0;
            Q0 = qSketchRegion(id + "F36", true);
            extrude(context, id + "F37", {"entities" : qUnion([Q0]), "operationType" : NewBodyOperationType.REMOVE, "oppositeDirection" : true, "depth" : 70 * mm});
        }
        {
            var Q0;
            Q0=qCreatedBy(id+"F35.planeOp",FACE);
            var sketch = newSketch(context, id + "F38", { "sketchPlane" : qUnion([Q0])});
            skLineSegment(sketch, "E99.0", {"start": v(6.56, -82) * mm, "end": v(33.44, -82) * mm});
            skArc(sketch, "E100", {"start": v(-50, -12) * mm, "mid": v(20, -82) * mm, "end": v(90, -12) * mm});
            skPoint(sketch, "E100.centerSnap0", {"position": v(20, -82) * mm});
            skArc(sketch, "E101.0", {"start": v(-46, -12) * mm, "mid": v(20, -78) * mm, "end": v(86, -12) * mm});
            skLineSegment(sketch, "E102", {"start": v(-46, -12) * mm, "end": v(-50, -12) * mm});
            skLineSegment(sketch, "E103", {"start": v(86, -12) * mm, "end": v(90, -12) * mm});
            skSolve(sketch);
        }
        {
            var Q0;
            Q0 = qSketchRegion(id + "F38", true);
            extrude(context, id + "F39", {"entities" : qUnion([Q0]), "oppositeDirection" : true, "depth" : 70 * mm});
        }
    });
